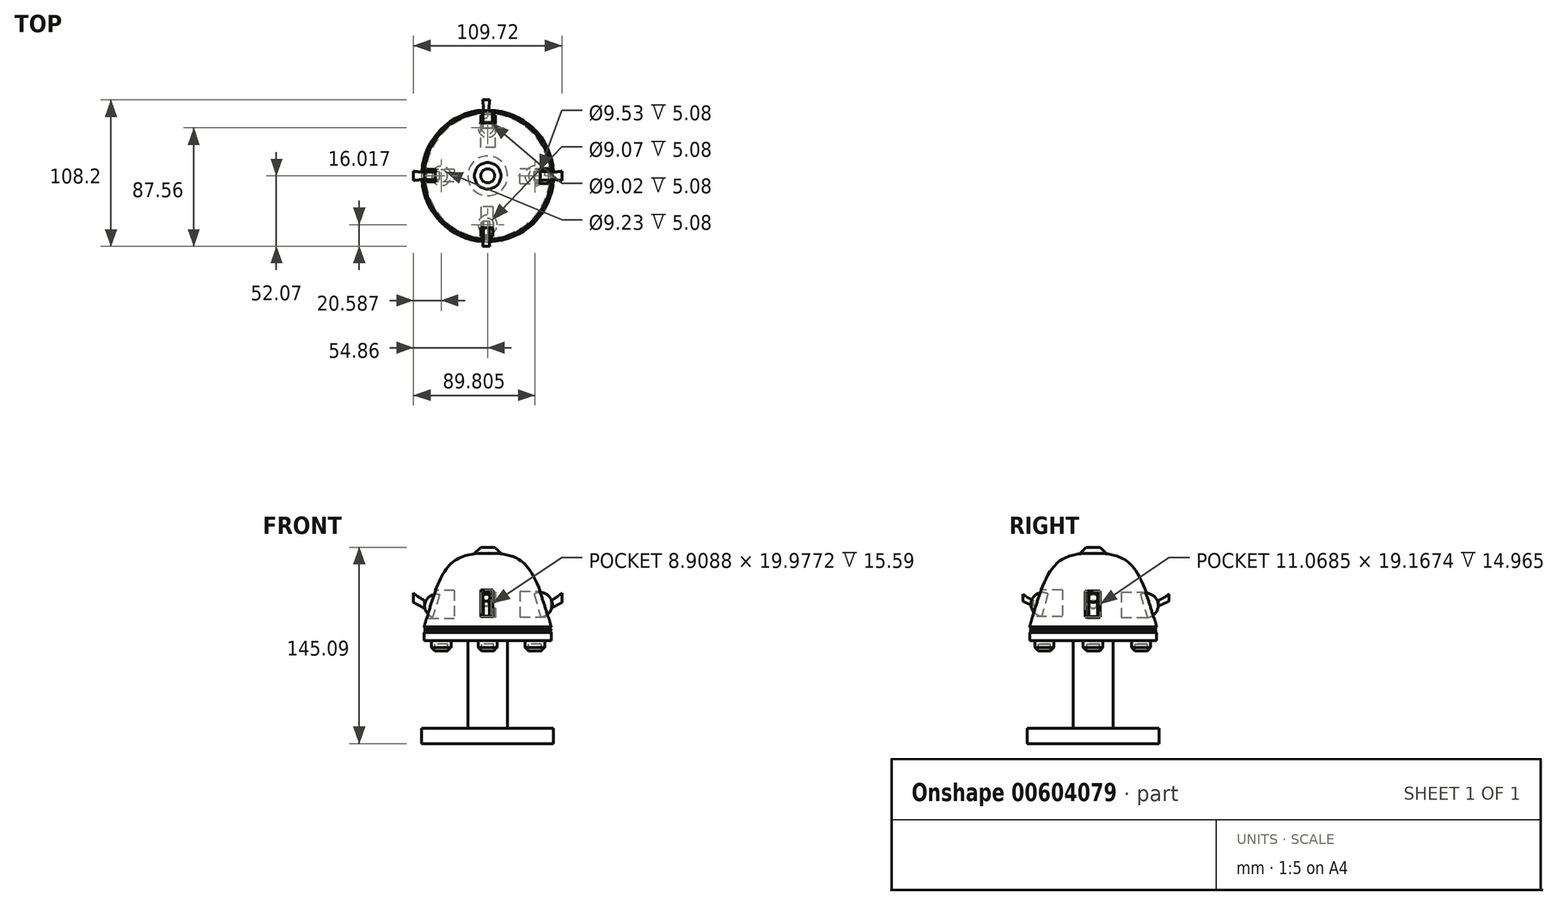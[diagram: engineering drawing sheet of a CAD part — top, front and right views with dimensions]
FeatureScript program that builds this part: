
annotation { "Feature Type Name" : "Feature", "Feature Type Description" : "" }
export const myFeature = defineFeature(function(context is Context, id is Id, definition is map)
    precondition{}
    {
        {
            var Q0;
            Q0=qCreatedBy(makeId("Front.planeOp"),FACE);
            var sketch = newSketch(context, id + "F0", { "sketchPlane" : qUnion([Q0])});
            skLineSegment(sketch, "E0", {"start": v(0, 53.19) * mm, "end": v(0, -53.67) * mm});
            skLineSegment(sketch, "E1", {"start": v(-46.96, -41.02) * mm, "end": v(-46.96, -39.5) * mm});
            skLineSegment(sketch, "E2", {"start": v(-46.96, 0) * mm, "end": v(-46.96, 10.12) * mm});
            skFitSpline(sketch, "E3", {"points": [v(-46.96, 10.12) * mm, v(-26.34, 57.46) * mm, v(0, 64.89) * mm], "startDerivative": vector(27.85, 100.38) * mm, "endDerivative": vector(68.18, 4.1) * mm});
            skLineSegment(sketch, "E4", {"start": v(0, 64.89) * mm, "end": v(0, 53.19) * mm});
            skLineSegment(sketch, "E5", {"start": v(-46.96, 0) * mm, "end": v(-14.7, 0) * mm});
            skLineSegment(sketch, "E6", {"start": v(-14.7, 0) * mm, "end": v(-14.7, -41.02) * mm});
            skLineSegment(sketch, "E7", {"start": v(-46.96, 10.12) * mm, "end": v(-45.93, 9.09) * mm});
            skLineSegment(sketch, "E8", {"start": v(-45.93, 9.09) * mm, "end": v(-46.96, 8.06) * mm});
            skLineSegment(sketch, "E9", {"start": v(-46.96, 8.06) * mm, "end": v(-45.93, 7.03) * mm});
            skLineSegment(sketch, "E10", {"start": v(-45.93, 7.03) * mm, "end": v(-46.96, 6) * mm});
            skLineSegment(sketch, "E11", {"start": v(-14.7, -41.02) * mm, "end": v(-14.7, -64.92) * mm});
            skLineSegment(sketch, "E12", {"start": v(-14.7, -64.92) * mm, "end": v(-48.74, -64.92) * mm});
            skLineSegment(sketch, "E13", {"start": v(-48.74, -64.92) * mm, "end": v(-48.74, -76.26) * mm});
            skLineSegment(sketch, "E14", {"start": v(-48.74, -76.26) * mm, "end": v(0, -76.26) * mm});
            skLineSegment(sketch, "E15", {"start": v(0, -76.26) * mm, "end": v(0, -8.2) * mm});
            skPoint(sketch, "E16.end.orphan", {"position": v(-46.96, -41.02) * mm});
            skSolve(sketch);
        }
        {
            var Q0;
            Q0=makeQuery(id+"F0.imprint","IMPRINT",FACE,{"disambiguationData":[TD([[makeQuery(id+"F0.imprint","IMPRINT",EDGE,{"derivedFrom":sQuery(id+"F0.wireOp",EDGE,"E0")}),-1.0]])]});
            var Q1;
            Q1=sQuery(id+"F0.wireOp",EDGE,"E0");
            revolve(context, id + "F1", {"entities" : qUnion([Q0]), "axis" : qUnion([Q1]), "revolveType" : RevolveType.FULL});
        }
        {
            var Q0;
            Q0=qCreatedBy(makeId("Front.planeOp"),FACE);
            cPlane(context, id + "F2", {"entities" : qUnion([Q0]), "cplaneType" : CPlaneType.OFFSET, "offset" : 48.26 * mm, "width" : 152.4 * mm, "height" : 152.4 * mm});
        }
        {
            var Q0;
            Q0=qCreatedBy(id+"F2.planeOp",FACE);
            var sketch = newSketch(context, id + "F3", { "sketchPlane" : qUnion([Q0])});
            skLineSegment(sketch, "E17.bottom", {"start": v(3.91, 37.5) * mm, "end": v(-5, 37.5) * mm});
            skLineSegment(sketch, "E17.top", {"start": v(3.91, 17.52) * mm, "end": v(-5, 17.52) * mm});
            skLineSegment(sketch, "E17.left", {"start": v(3.91, 37.5) * mm, "end": v(3.91, 17.52) * mm});
            skLineSegment(sketch, "E17.right", {"start": v(-5, 37.5) * mm, "end": v(-5, 17.52) * mm});
            skSolve(sketch);
        }
        {
            var Q0;
            Q0 = qSketchRegion(id + "F3", true);
            extrude(context, id + "F4", {"entities" : qUnion([Q0]), "operationType" : NewBodyOperationType.REMOVE, "oppositeDirection" : true, "depth" : 25.4 * mm, "offsetDistance" : 25.4 * mm});
        }
        {
            var Q0;
            Q0=qCreatedBy(makeId("Right.planeOp"),FACE);
            cPlane(context, id + "F5", {"entities" : qUnion([Q0]), "cplaneType" : CPlaneType.OFFSET, "offset" : 1.02 * mm, "oppositeDirection" : true, "width" : 152.4 * mm, "height" : 152.4 * mm});
        }
        {
            var Q0;
            Q0=qCreatedBy(id+"F5.planeOp",FACE);
            var sketch = newSketch(context, id + "F6", { "sketchPlane" : qUnion([Q0])});
            skLineSegment(sketch, "E18", {"start": v(-33.61, 34.52) * mm, "end": v(-37.93, 18.06) * mm});
            skArc(sketch, "E19", {"start": v(-33.61, 34.52) * mm, "mid": v(-45.75, 28.9) * mm, "end": v(-37.93, 18.06) * mm});
            skSolve(sketch);
        }
        {
            var Q0;
            Q0 = qSketchRegion(id + "F6", true);
            extrude(context, id + "F7", {"entities" : qUnion([Q0]), "depth" : 4.57 * mm, "offsetDistance" : 25.4 * mm, "symmetric" : true});
        }
        {
            var Q0;
            Q0=qCreatedBy(id+"F5.planeOp",FACE);
            cPlane(context, id + "F8", {"entities" : qUnion([Q0]), "cplaneType" : CPlaneType.OFFSET, "offset" : 45.97 * mm, "oppositeDirection" : true, "width" : 152.4 * mm, "height" : 152.4 * mm});
        }
        {
            var Q0;
            Q0=qCreatedBy(id+"F8.planeOp",FACE);
            var sketch = newSketch(context, id + "F9", { "sketchPlane" : qUnion([Q0])});
            skLineSegment(sketch, "E20.bottom", {"start": v(4.72, 36.95) * mm, "end": v(-4.45, 36.95) * mm});
            skLineSegment(sketch, "E20.top", {"start": v(4.72, 16.17) * mm, "end": v(-4.45, 16.17) * mm});
            skLineSegment(sketch, "E20.left", {"start": v(4.72, 36.95) * mm, "end": v(4.72, 16.17) * mm});
            skLineSegment(sketch, "E20.right", {"start": v(-4.45, 36.95) * mm, "end": v(-4.45, 16.17) * mm});
            skSolve(sketch);
        }
        {
            var Q0;
            Q0 = qSketchRegion(id + "F9", true);
            extrude(context, id + "F10", {"entities" : qUnion([Q0]), "operationType" : NewBodyOperationType.REMOVE, "depth" : 22.35 * mm, "offsetDistance" : 25.4 * mm});
        }
        {
            var Q0;
            Q0=qCreatedBy(makeId("Front.planeOp"),FACE);
            var sketch = newSketch(context, id + "F11", { "sketchPlane" : qUnion([Q0])});
            skLineSegment(sketch, "E21", {"start": v(-35.5, 33.71) * mm, "end": v(-40.63, 17.25) * mm});
            skArc(sketch, "E22", {"start": v(-35.5, 33.71) * mm, "mid": v(-46.19, 28) * mm, "end": v(-40.63, 17.25) * mm});
            skSolve(sketch);
        }
        {
            var Q0;
            Q0 = qSketchRegion(id + "F11", true);
            extrude(context, id + "F12", {"entities" : qUnion([Q0]), "depth" : 5.6 * mm, "offsetDistance" : 25.4 * mm, "symmetric" : true});
        }
        {
            var Q0;
            Q0=qCreatedBy(id+"F8.planeOp",FACE);
            cPlane(context, id + "F13", {"entities" : qUnion([Q0]), "cplaneType" : CPlaneType.OFFSET, "offset" : 96.27 * mm, "width" : 152.4 * mm, "height" : 152.4 * mm});
        }
        {
            var Q0;
            Q0=qCreatedBy(id+"F13.planeOp",FACE);
            var sketch = newSketch(context, id + "F14", { "sketchPlane" : qUnion([Q0])});
            skLineSegment(sketch, "E23.bottom", {"start": v(-5.8, 36.41) * mm, "end": v(5.26, 36.41) * mm});
            skLineSegment(sketch, "E23.top", {"start": v(-5.8, 17.25) * mm, "end": v(5.26, 17.25) * mm});
            skLineSegment(sketch, "E23.left", {"start": v(-5.8, 36.41) * mm, "end": v(-5.8, 17.25) * mm});
            skLineSegment(sketch, "E23.right", {"start": v(5.26, 36.41) * mm, "end": v(5.26, 17.25) * mm});
            skSolve(sketch);
        }
        {
            var Q0;
            Q0 = qSketchRegion(id + "F14", true);
            extrude(context, id + "F15", {"entities" : qUnion([Q0]), "operationType" : NewBodyOperationType.REMOVE, "oppositeDirection" : true, "depth" : 25.4 * mm, "offsetDistance" : 25.4 * mm});
        }
        {
            var Q0;
            Q0=qCreatedBy(makeId("Front.planeOp"),FACE);
            var sketch = newSketch(context, id + "F16", { "sketchPlane" : qUnion([Q0])});
            skLineSegment(sketch, "E24", {"start": v(34.42, 34.25) * mm, "end": v(39, 17.52) * mm});
            skArc(sketch, "E25", {"start": v(39, 17.52) * mm, "mid": v(47.5, 28.84) * mm, "end": v(34.42, 34.25) * mm});
            skSolve(sketch);
        }
        {
            var Q0;
            Q0 = qSketchRegion(id + "F16", true);
            extrude(context, id + "F17", {"entities" : qUnion([Q0]), "depth" : 6.6 * mm, "offsetDistance" : 25.4 * mm, "symmetric" : true});
        }
        {
            var Q0;
            Q0=qCreatedBy(makeId("Front.planeOp"),FACE);
            cPlane(context, id + "F18", {"entities" : qUnion([Q0]), "cplaneType" : CPlaneType.OFFSET, "offset" : 49.78 * mm, "oppositeDirection" : true, "width" : 152.4 * mm, "height" : 152.4 * mm});
        }
        {
            var Q0;
            Q0=qCreatedBy(id+"F18.planeOp",FACE);
            var sketch = newSketch(context, id + "F19", { "sketchPlane" : qUnion([Q0])});
            skLineSegment(sketch, "E26.bottom", {"start": v(5.8, 35.6) * mm, "end": v(-5, 35.6) * mm});
            skLineSegment(sketch, "E26.top", {"start": v(5.8, 16.98) * mm, "end": v(-5, 16.98) * mm});
            skLineSegment(sketch, "E26.left", {"start": v(5.8, 35.6) * mm, "end": v(5.8, 16.98) * mm});
            skLineSegment(sketch, "E26.right", {"start": v(-5, 35.6) * mm, "end": v(-5, 16.98) * mm});
            skSolve(sketch);
        }
        {
            var Q0;
            Q0 = qSketchRegion(id + "F19", true);
            extrude(context, id + "F20", {"entities" : qUnion([Q0]), "operationType" : NewBodyOperationType.REMOVE, "depth" : 28.96 * mm, "offsetDistance" : 25.4 * mm});
        }
        {
            var Q0;
            Q0=qCreatedBy(makeId("Right.planeOp"),FACE);
            var sketch = newSketch(context, id + "F21", { "sketchPlane" : qUnion([Q0])});
            skLineSegment(sketch, "E27", {"start": v(34.94, 33.98) * mm, "end": v(40.07, 16.98) * mm});
            skArc(sketch, "E28", {"start": v(40.07, 16.98) * mm, "mid": v(47.7, 28.55) * mm, "end": v(34.94, 33.98) * mm});
            skSolve(sketch);
        }
        {
            var Q0;
            Q0 = qSketchRegion(id + "F21", true);
            extrude(context, id + "F22", {"entities" : qUnion([Q0]), "depth" : 7.11 * mm, "offsetDistance" : 25.4 * mm, "symmetric" : true});
        }
        {
            var Q0;
            Q0=qCreatedBy(makeId("Top.planeOp"),FACE);
            var sketch = newSketch(context, id + "F23", { "sketchPlane" : qUnion([Q0])});
            skCircle(sketch, "E29", {"center": v(-34.27, 0) * mm, "radius": 7.15 * mm});
            skSolve(sketch);
        }
        {
            var Q0;
            Q0 = qSketchRegion(id + "F23", true);
            extrude(context, id + "F24", {"entities" : qUnion([Q0]), "oppositeDirection" : true, "depth" : 10.16 * mm, "offsetDistance" : 25.4 * mm});
        }
        {
            var Q0;
            Q0=makeQuery(id+"F24.opExtrude","CAP_FACE",FACE,{"disambiguationData":[OSD([sQuery(id+"F23.wireOp",EDGE,"E29")])],"isStart":false});
            shell(context, id + "F25", {"entities" : qUnion([Q0]), "thickness" : 2.54 * mm});
        }
        {
            var Q0;
            Q0=makeQuery(id+"F24.opExtrude","CAP_EDGE",EDGE,{"disambiguationData":[OSD([sQuery(id+"F23.wireOp",EDGE,"E29")])],"isStart":false});
            chamfer(context, id + "F26", {"entities" : qUnion([Q0]), "width" : 5.08 * mm, "tangentPropagation" : true});
        }
        {
            var Q0;
            Q0=qCreatedBy(makeId("Top.planeOp"),FACE);
            var sketch = newSketch(context, id + "F27", { "sketchPlane" : qUnion([Q0])});
            skCircle(sketch, "E30", {"center": v(34.95, 0) * mm, "radius": 7.3 * mm});
            skSolve(sketch);
        }
        {
            var Q0;
            Q0 = qSketchRegion(id + "F27", true);
            extrude(context, id + "F28", {"entities" : qUnion([Q0]), "oppositeDirection" : true, "depth" : 10.16 * mm, "offsetDistance" : 25.4 * mm});
        }
        {
            var Q0;
            Q0=makeQuery(id+"F28.opExtrude","CAP_FACE",FACE,{"disambiguationData":[OSD([sQuery(id+"F27.wireOp",EDGE,"E30")])],"isStart":false});
            shell(context, id + "F29", {"entities" : qUnion([Q0]), "thickness" : 2.54 * mm});
        }
        {
            var Q0;
            Q0=makeQuery(id+"F28.opExtrude","CAP_EDGE",EDGE,{"disambiguationData":[OSD([sQuery(id+"F27.wireOp",EDGE,"E30")])],"isStart":false});
            chamfer(context, id + "F30", {"entities" : qUnion([Q0]), "width" : 5.08 * mm, "tangentPropagation" : true});
        }
        {
            var Q0;
            Q0=qCreatedBy(makeId("Top.planeOp"),FACE);
            var sketch = newSketch(context, id + "F31", { "sketchPlane" : qUnion([Q0])});
            skCircle(sketch, "E31", {"center": v(0, 35.5) * mm, "radius": 7.05 * mm});
            skSolve(sketch);
        }
        {
            var Q0;
            Q0 = qSketchRegion(id + "F31", true);
            extrude(context, id + "F32", {"entities" : qUnion([Q0]), "oppositeDirection" : true, "depth" : 10.16 * mm, "offsetDistance" : 25.4 * mm});
        }
        {
            var Q0;
            Q0=makeQuery(id+"F32.opExtrude","CAP_FACE",FACE,{"disambiguationData":[OSD([sQuery(id+"F31.wireOp",EDGE,"E31")])],"isStart":false});
            shell(context, id + "F33", {"entities" : qUnion([Q0]), "thickness" : 2.54 * mm});
        }
        {
            var Q0;
            Q0=makeQuery(id+"F32.opExtrude","CAP_EDGE",EDGE,{"disambiguationData":[OSD([sQuery(id+"F31.wireOp",EDGE,"E31")])],"isStart":false});
            chamfer(context, id + "F34", {"entities" : qUnion([Q0]), "width" : 5.08 * mm, "tangentPropagation" : true});
        }
        {
            var Q0;
            Q0=qCreatedBy(makeId("Top.planeOp"),FACE);
            var sketch = newSketch(context, id + "F35", { "sketchPlane" : qUnion([Q0])});
            skCircle(sketch, "E32", {"center": v(0, -36.05) * mm, "radius": 7.07 * mm});
            skSolve(sketch);
        }
        {
            var Q0;
            Q0 = qSketchRegion(id + "F35", true);
            extrude(context, id + "F36", {"entities" : qUnion([Q0]), "oppositeDirection" : true, "depth" : 10.16 * mm, "offsetDistance" : 25.4 * mm});
        }
        {
            var Q0;
            Q0=makeQuery(id+"F36.opExtrude","CAP_FACE",FACE,{"disambiguationData":[OSD([sQuery(id+"F35.wireOp",EDGE,"E32")])],"isStart":false});
            shell(context, id + "F37", {"entities" : qUnion([Q0]), "thickness" : 2.54 * mm});
        }
        {
            var Q0;
            Q0=makeQuery(id+"F36.opExtrude","CAP_EDGE",EDGE,{"disambiguationData":[OSD([sQuery(id+"F35.wireOp",EDGE,"E32")])],"isStart":false});
            chamfer(context, id + "F38", {"entities" : qUnion([Q0]), "width" : 5.08 * mm, "tangentPropagation" : true});
        }
        {
            var Q0;
            Q0=qCreatedBy(makeId("Top.planeOp"),FACE);
            cPlane(context, id + "F39", {"entities" : qUnion([Q0]), "cplaneType" : CPlaneType.OFFSET, "offset" : 64.26 * mm, "width" : 152.4 * mm, "height" : 152.4 * mm});
        }
        {
            var Q0;
            Q0=qCreatedBy(id+"F39.planeOp",FACE);
            var sketch = newSketch(context, id + "F40", { "sketchPlane" : qUnion([Q0])});
            skCircle(sketch, "E33", {"center": v(0, 0) * mm, "radius": 10.3 * mm});
            skSolve(sketch);
        }
        {
            var Q0;
            Q0 = qSketchRegion(id + "F40", true);
            extrude(context, id + "F41", {"entities" : qUnion([Q0]), "depth" : 4.57 * mm, "offsetDistance" : 25.4 * mm});
        }
        {
            var Q0;
            Q0=makeQuery(id+"F41.opExtrude","CAP_EDGE",EDGE,{"disambiguationData":[OSD([sQuery(id+"F40.wireOp",EDGE,"E33")])],"isStart":false});
            chamfer(context, id + "F42", {"entities" : qUnion([Q0]), "width" : 5.08 * mm, "tangentPropagation" : true});
        }
        {
            var Q0;
            Q0=qCreatedBy(id+"F2.planeOp",FACE);
            cPlane(context, id + "F43", {"entities" : qUnion([Q0]), "cplaneType" : CPlaneType.OFFSET, "offset" : 4.32 * mm, "oppositeDirection" : true, "width" : 152.4 * mm, "height" : 152.4 * mm});
        }
        {
            var Q0;
            Q0=qCreatedBy(id+"F2.planeOp",FACE);
            cPlane(context, id + "F44", {"entities" : qUnion([Q0]), "cplaneType" : CPlaneType.OFFSET, "offset" : 3.8 * mm, "width" : 152.4 * mm, "height" : 152.4 * mm});
        }
        {
            var Q0;
            Q0=qCreatedBy(id+"F43.planeOp",FACE);
            var sketch = newSketch(context, id + "F45", { "sketchPlane" : qUnion([Q0])});
            skCircle(sketch, "E34", {"center": v(-1.1, 27.43) * mm, "radius": 2.09 * mm});
            skSolve(sketch);
        }
        {
            var Q0;
            Q0=qCreatedBy(id+"F2.planeOp",FACE);
            var sketch = newSketch(context, id + "F46", { "sketchPlane" : qUnion([Q0])});
            skCircle(sketch, "E35", {"center": v(-1.1, 29.49) * mm, "radius": 2.2 * mm});
            skSolve(sketch);
        }
        {
            var Q0;
            Q0=qCreatedBy(id+"F44.planeOp",FACE);
            var sketch = newSketch(context, id + "F47", { "sketchPlane" : qUnion([Q0])});
            skCircle(sketch, "E36", {"center": v(-1.1, 31.68) * mm, "radius": 2.63 * mm});
            skSolve(sketch);
        }
        {
            var Q1;
            Q1 = qSketchRegion(id + "F45", true);
            var Q2;
            Q2 = qSketchRegion(id + "F46", true);
            var Q3;
            Q3 = qSketchRegion(id + "F47", true);
            loft(context, id + "F48", {"sheetProfilesArray" : [{ "sheetProfileEntities" : qUnion([Q1]) }, { "sheetProfileEntities" : qUnion([Q2]) }, { "sheetProfileEntities" : qUnion([Q3]) }]});
        }
        {
            var Q0;
            Q0=qCreatedBy(makeId("Front.planeOp"),FACE);
            cPlane(context, id + "F49", {"entities" : qUnion([Q0]), "cplaneType" : CPlaneType.OFFSET, "offset" : 2.03 * mm, "oppositeDirection" : true, "width" : 152.4 * mm, "height" : 152.4 * mm});
        }
        {
            var Q0;
            Q0=makeQuery(id+"F48.opLoft","SWEPT_BODY",BODY,{"disambiguationData":[OSD([makeQuery(id+"F45.imprint","IMPRINT",FACE,{"disambiguationData":[TD([[makeQuery(id+"F45.imprint","IMPRINT",EDGE,{"derivedFrom":sQuery(id+"F45.wireOp",EDGE,"E34")}),1.0]])]}),sQuery(id+"F46.wireOp",EDGE,"E35"),makeQuery(id+"F47.imprint","IMPRINT",FACE,{"disambiguationData":[TD([[makeQuery(id+"F47.imprint","IMPRINT",EDGE,{"derivedFrom":sQuery(id+"F47.wireOp",EDGE,"E36")}),1.0]])]})])]});
            var Q1;
            Q1=qCreatedBy(id+"F49.planeOp",FACE);
            mirror(context, id + "F50", {"entities" : qUnion([Q0]), "mirrorPlane" : qUnion([Q1])});
        }
        {
            var Q0;
            Q0=qCreatedBy(makeId("Right.planeOp"),FACE);
            cPlane(context, id + "F51", {"entities" : qUnion([Q0]), "cplaneType" : CPlaneType.OFFSET, "offset" : 46.74 * mm, "width" : 152.4 * mm, "height" : 152.4 * mm});
        }
        {
            var Q0;
            Q0=qCreatedBy(id+"F51.planeOp",FACE);
            cPlane(context, id + "F52", {"entities" : qUnion([Q0]), "cplaneType" : CPlaneType.OFFSET, "offset" : 4.57 * mm, "width" : 152.4 * mm, "height" : 152.4 * mm});
        }
        {
            var Q0;
            Q0=qCreatedBy(id+"F52.planeOp",FACE);
            cPlane(context, id + "F53", {"entities" : qUnion([Q0]), "cplaneType" : CPlaneType.OFFSET, "offset" : 3.56 * mm, "width" : 152.4 * mm, "height" : 152.4 * mm});
        }
        {
            var Q0;
            Q0=qCreatedBy(id+"F51.planeOp",FACE);
            var sketch = newSketch(context, id + "F54", { "sketchPlane" : qUnion([Q0])});
            skCircle(sketch, "E37", {"center": v(0, 26.61) * mm, "radius": 2.94 * mm});
            skSolve(sketch);
        }
        {
            var Q0;
            Q0=qCreatedBy(id+"F52.planeOp",FACE);
            var sketch = newSketch(context, id + "F55", { "sketchPlane" : qUnion([Q0])});
            skCircle(sketch, "E38", {"center": v(0, 29.29) * mm, "radius": 3.02 * mm});
            skSolve(sketch);
        }
        {
            var Q0;
            Q0=qCreatedBy(id+"F53.planeOp",FACE);
            var sketch = newSketch(context, id + "F56", { "sketchPlane" : qUnion([Q0])});
            skCircle(sketch, "E39", {"center": v(0, 31.58) * mm, "radius": 3.44 * mm});
            skSolve(sketch);
        }
        {
            var Q1;
            Q1 = qSketchRegion(id + "F54", true);
            var Q2;
            Q2 = qSketchRegion(id + "F55", true);
            var Q3;
            Q3 = qSketchRegion(id + "F56", true);
            loft(context, id + "F57", {"sheetProfilesArray" : [{ "sheetProfileEntities" : qUnion([Q1]) }, { "sheetProfileEntities" : qUnion([Q2]) }, { "sheetProfileEntities" : qUnion([Q3]) }]});
        }
        {
            var Q0;
            Q0=qCreatedBy(id+"F52.planeOp",FACE);
            cPlane(context, id + "F58", {"entities" : qUnion([Q0]), "cplaneType" : CPlaneType.OFFSET, "offset" : 51.3 * mm, "oppositeDirection" : true, "width" : 152.4 * mm, "height" : 152.4 * mm});
        }
        {
            var Q0;
            Q0=makeQuery(id+"F57.opLoft","SWEPT_BODY",BODY,{"disambiguationData":[OSD([makeQuery(id+"F54.imprint","IMPRINT",FACE,{"disambiguationData":[TD([[makeQuery(id+"F54.imprint","IMPRINT",EDGE,{"derivedFrom":sQuery(id+"F54.wireOp",EDGE,"E37")}),1.0]])]}),sQuery(id+"F55.wireOp",EDGE,"E38"),makeQuery(id+"F56.imprint","IMPRINT",FACE,{"disambiguationData":[TD([[makeQuery(id+"F56.imprint","IMPRINT",EDGE,{"derivedFrom":sQuery(id+"F56.wireOp",EDGE,"E39")}),1.0]])]})])]});
            var Q1;
            Q1=qCreatedBy(id+"F58.planeOp",FACE);
            mirror(context, id + "F59", {"entities" : qUnion([Q0]), "mirrorPlane" : qUnion([Q1])});
        }
    });
